# Revit family: CABINET02
name_source: partatom
category: Generic Models
revit_build: Autodesk Revit Architecture 2014 (Build: 20130308_1515(x64)
units: mm (PartAtom-declared; Revit-internal decimal feet)

## types (1)
- CABINET02
    depth = 622 mm  [stored 2.04068 ft]
    depth_gbl = 600 mm
    door_code = 603 mm
    gap_btm = 2 mm  [stored 0.00656168 ft]
    gap_door = 3 mm  [stored 0.00984252 ft]
    gap_left = 1 mm  [stored 0.00328084 ft]
    gap_right = 1 mm  [stored 0.00328084 ft]
    gap_top = 5 mm  [stored 0.0164042 ft]
    height = 748 mm  [stored 2.45407 ft]
    kick = 134 mm  [stored 0.439633 ft]
    rails = 460 mm
    thickness_back_material = 16 mm  [stored 0.0524934 ft]
    thickness_door = 19 mm  [stored 0.062336 ft]
    thickness_material = 19 mm  [stored 0.062336 ft]
    thickness_material_minus = -19 mm  [stored -0.062336 ft]
    width = 600 mm

note: [stored X ft] marks values corroborated as IEEE doubles in the binary element streams (Revit-internal decimal feet)

## geometry (parser evidence)
native form markers: Sweep x1
no freeform markers — native parametric forms only
